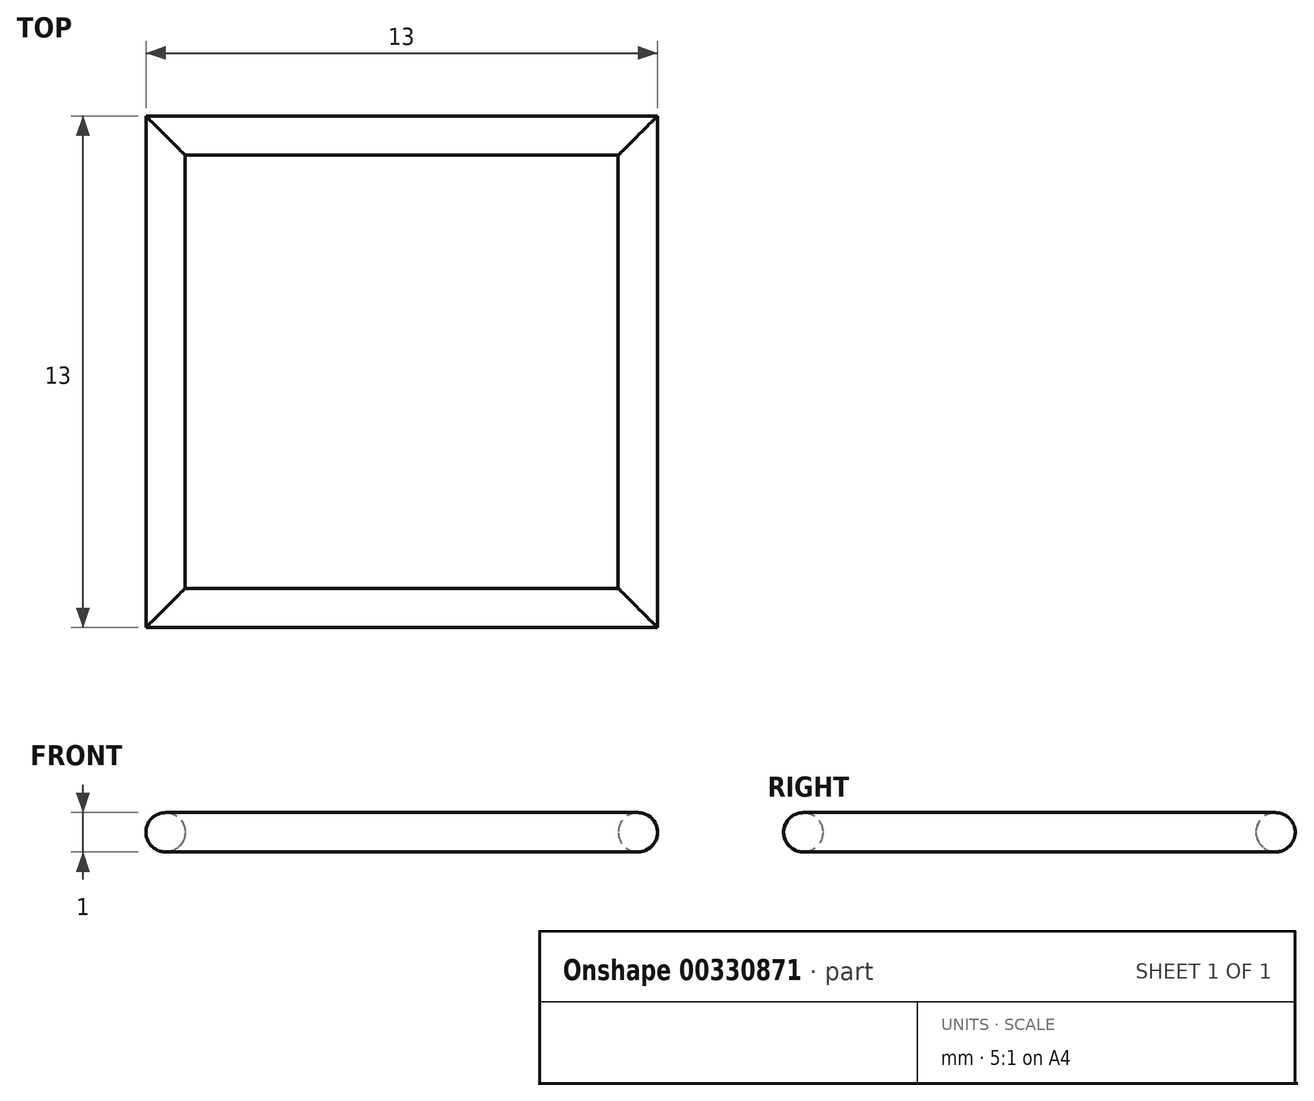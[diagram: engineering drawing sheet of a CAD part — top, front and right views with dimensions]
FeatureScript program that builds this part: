
annotation { "Feature Type Name" : "Feature", "Feature Type Description" : "" }
export const myFeature = defineFeature(function(context is Context, id is Id, definition is map)
    precondition{}
    {
        {
            var Q0;
            Q0=qCreatedBy(makeId("Top.planeOp"),FACE);
            var sketch = newSketch(context, id + "F0", { "sketchPlane" : qUnion([Q0])});
            skLineSegment(sketch, "E0.bottom", {"start": v(-6, -6) * mm, "end": v(6, -6) * mm});
            skLineSegment(sketch, "E0.top", {"start": v(-6, 6) * mm, "end": v(6, 6) * mm});
            skLineSegment(sketch, "E0.left", {"start": v(-6, -6) * mm, "end": v(-6, 6) * mm});
            skLineSegment(sketch, "E0.right", {"start": v(6, -6) * mm, "end": v(6, 6) * mm});
            skPoint(sketch, "E0.middle", {"position": v(0, 0) * mm});
            skSolve(sketch);
        }
        {
            var Q0;
            Q0=qCreatedBy(makeId("Front.planeOp"),FACE);
            var sketch = newSketch(context, id + "F1", { "sketchPlane" : qUnion([Q0])});
            skCircle(sketch, "E1", {"center": v(6, 0) * mm, "radius": 0.5 * mm});
            skSolve(sketch);
        }
        {
            var Q0;
            Q0=makeQuery(id+"F1.imprint","IMPRINT",FACE,{"disambiguationData":[TD([[makeQuery(id+"F1.imprint","IMPRINT",EDGE,{"derivedFrom":sQuery(id+"F1.wireOp",EDGE,"E1")}),1.0]])]});
            var Q1;
            Q1=sQuery(id+"F1.wireOp",EDGE,"E1");
            var Q2;
            Q2=sQuery(id+"F0.wireOp",EDGE,"E0.right");
            var Q3;
            Q3=sQuery(id+"F0.wireOp",EDGE,"E0.top");
            var Q4;
            Q4=sQuery(id+"F0.wireOp",EDGE,"E0.left");
            var Q5;
            Q5=sQuery(id+"F0.wireOp",EDGE,"E0.bottom");
            sweep(context, id + "F2", {"profiles" : qUnion([Q0]), "surfaceProfiles" : qUnion([Q1]), "path" : qUnion([Q2, Q3, Q4, Q5])});
        }
    });
